# Revit family: Condensing-Storage-Water-Heater-Gas_AO_Smith-BFC_28_PN
name_source: partatom
category: Mechanical Equipment
revit_build: Autodesk Revit 2014 (Build: 20140709_2115(x64)
units: mm (PartAtom-declared; Revit-internal decimal feet)

## types (1)
- Condensing-Storage-Water-Heater-Gas_AO_Smith-BFC_28_PN
    (Additional Control) Frequency = 0 Hz
    (Additional Control) Phase = 1
    (Additional Control) Power Consumption (nominal) = 0 W
    (Additional Control) Voltage = 0 V
    1e Maintenance (check-up) = 3 maanden na installatie
    2nd Maintenance (general maintenance) = 12 maanden na installatie
    APS Pressure < = 115.0 Pa
    Assembly Code = D3010
    BIM Content Developer = CAD & Company
    CE-PIN = 0063BU3889
    Co2 Emissions (tol. +/- 1.0) vol% = 12.0/10.0
    Cold Water Connection R = 1 1/2"
    Condens Discharge Connection = 40 mm  [stored 0.131234 ft]
    Default Setpoint = 65 °C
    Description = Condenserende Hoog Rendementsboiler
    Destination / Country = Nederland
    Diameter = 705 mm  [stored 2.31299 ft]
    Drain Valve Connection Rp = 1"
    Draw-off Capacity @ ΔT = 28°C after 120 min. = 2200.0 L
    Draw-off Capacity @ ΔT = 28°C after 30 min. = 730.0 L
    Draw-off Capacity @ ΔT = 28°C after 60 min. = 1300.0 L
    Draw-off Capacity @ ΔT = 28°C after 90 min. = 1700.0 L
    Draw-off Capacity @ ΔT = 44°C after 120 min. = 1400.0 L
    Draw-off Capacity @ ΔT = 44°C after 30 min. = 430.0 L
    Draw-off Capacity @ ΔT = 44°C after 60 min. = 730.0 L
    Draw-off Capacity @ ΔT = 44°C after 90 min. = 1100.0 L
    Draw-off Capacity @ ΔT = 50°C after 120 min. = 1200.0 L
    Draw-off Capacity @ ΔT = 50°C after 30 min. = 360.0 L
    Draw-off Capacity @ ΔT = 50°C after 60 min. = 630.0 L
    Draw-off Capacity @ ΔT = 50°C after 90 min. = 900.0 L
    Draw-off Capacity @ ΔT = 55°C after 120 min. = 1100.0 L
    Draw-off Capacity @ ΔT = 55°C after 30 min. = 320.0 L
    Draw-off Capacity @ ΔT = 55°C after 60 min. = 560.0 L
    Draw-off Capacity @ ΔT = 55°C after 90 min. = 800.0 L
    Draw-off Capacity @ ΔT = 70°C after 120 min. = 790.0 L
    Draw-off Capacity @ ΔT = 70°C after 30 min. = 210.0 L
    Draw-off Capacity @ ΔT = 70°C after 60 min. = 400.0 L
    Draw-off Capacity @ ΔT = 70°C after 90 min. = 600.0 L
    Empty Weight = 177 kg
    Energy Efficiency Rating (Hi, acc NEN-EN 89-1999) = 107
    Energy Efficiency Rating (Hs, acc NEN-EN 89-1999) = 96
    Flue Diameter - concentric system = 100/150 mm/mm
    Flue Diameter - parallel system = 100 mm  [stored 0.328084 ft]
    Flue Diameter - water heater = 100/150 mm/mm
    Frequency = 50 Hz
    Gas Category = II2EK3B/P
    Gas Connection R = 3/4"
    Gas Flow Rate - Mass kg/h = 2.70/2.30
    Gas Flow Rate - Volume ltr/hr = 0
    Heating Up Time @ ΔT = 28°C = 14
    Heating Up Time @ ΔT = 44°C = 21
    Heating Up Time @ ΔT = 50°C = 24
    Heating Up Time @ ΔT = 55°C = 27
    Heating Up Time @ ΔT = 70°C = 34
    Height = 1390 mm  [stored 4.56037 ft]
    Height Air Inlet = 1365 mm  [stored 4.47835 ft]
    Height Cold water Intlet = 170 mm  [stored 0.557743 ft]
    Height Flue Outlet = 1365 mm  [stored 4.47835 ft]
    Height Gas Connection = 1285 mm  [stored 4.21588 ft]
    Height Warm Water Outlet = 1390 mm  [stored 4.56037 ft]
    Hot / Warm Water Connection R = 1 1/2"
    Installation Type = B23/C13/C33/C43/C53/C63
    Insulation Thickness = 50 mm  [stored 0.164042 ft]
    Length = 0 mm  [stored 0 ft]
    Maintenance Interval = 12 maanden
    Manufacturer = A.O. Smith Water Products Company b.v.
    Manufacturer Number = E 7110
    Max. Flue Gas Outlet Temperature = 45 °C
    Max. Operating Pressure = 800000.0 Pa
    Max. Setpoint = 80 °C
    Min. Setpoint = 40 °C
    Model = BFC 28 PN
    NOx Emissions (air free, 0% O2) ppm = 56.0/17.0
    NOx Emissions mg/kWh = 100.0/31.0
    Noice-level dB (A) = 45
    Nominal Heat Input (Gross) = 36800.0/32200.0
    Nominal Heat Input (Net) = 34000.0/29000.0
    Nominal Output = 36400.0/31000.0
    Operating Weight = 394 kg
    Packaging Height = 1550 mm  [stored 5.0853 ft]
    Packaging Length = 950 mm  [stored 3.1168 ft]
    Packaging Width = 790 mm  [stored 2.59186 ft]
    Phase = 1
    Power Consumption (nominal) = 45 W
    Product Documentation Link = https://www.aosmithinternational.com
    Product Instruction Link = https://www.aosmithinternational.com
    Recovery Rate @ ΔT = 28°C = 960.0 L/s
    Recovery Rate @ ΔT = 44°C = 610.0 L/s
    Recovery Rate @ ΔT = 50°C = 540.0 L/s
    Recovery Rate @ ΔT = 55°C = 490.0 L/s
    Recovery Rate @ ΔT = 70°C = 390.0 L/s
    Seasonal Energy Efficiency Rating = 96
    Serial Number = 8717449113070
    Stand-by Loss = 0 W
    Stand-by Loss - daily (24h) = 0 W
    Standard Set For = G30/G31
    Storage Capacity = 217.0 L
    Supply Pressure min/max = 3000 - 5000 Pa
    T&P Connection Rp = 1"
    Transport Weight = 196 kg
    Type of Packaging = Plastic Krimpverpakking, Karton en Hout
    URL = www.aosmith.nl
    Voltage = 230 V
    Warranty on parts = 12 maanden
    Warranty on tank = 36 maanden
    Width = 0 mm  [stored 0 ft]

note: [stored X ft] marks values corroborated as IEEE doubles in the binary element streams (Revit-internal decimal feet)

## geometry (parser evidence)
native form markers: Blend x20, Sweep x28
no freeform markers — native parametric forms only
